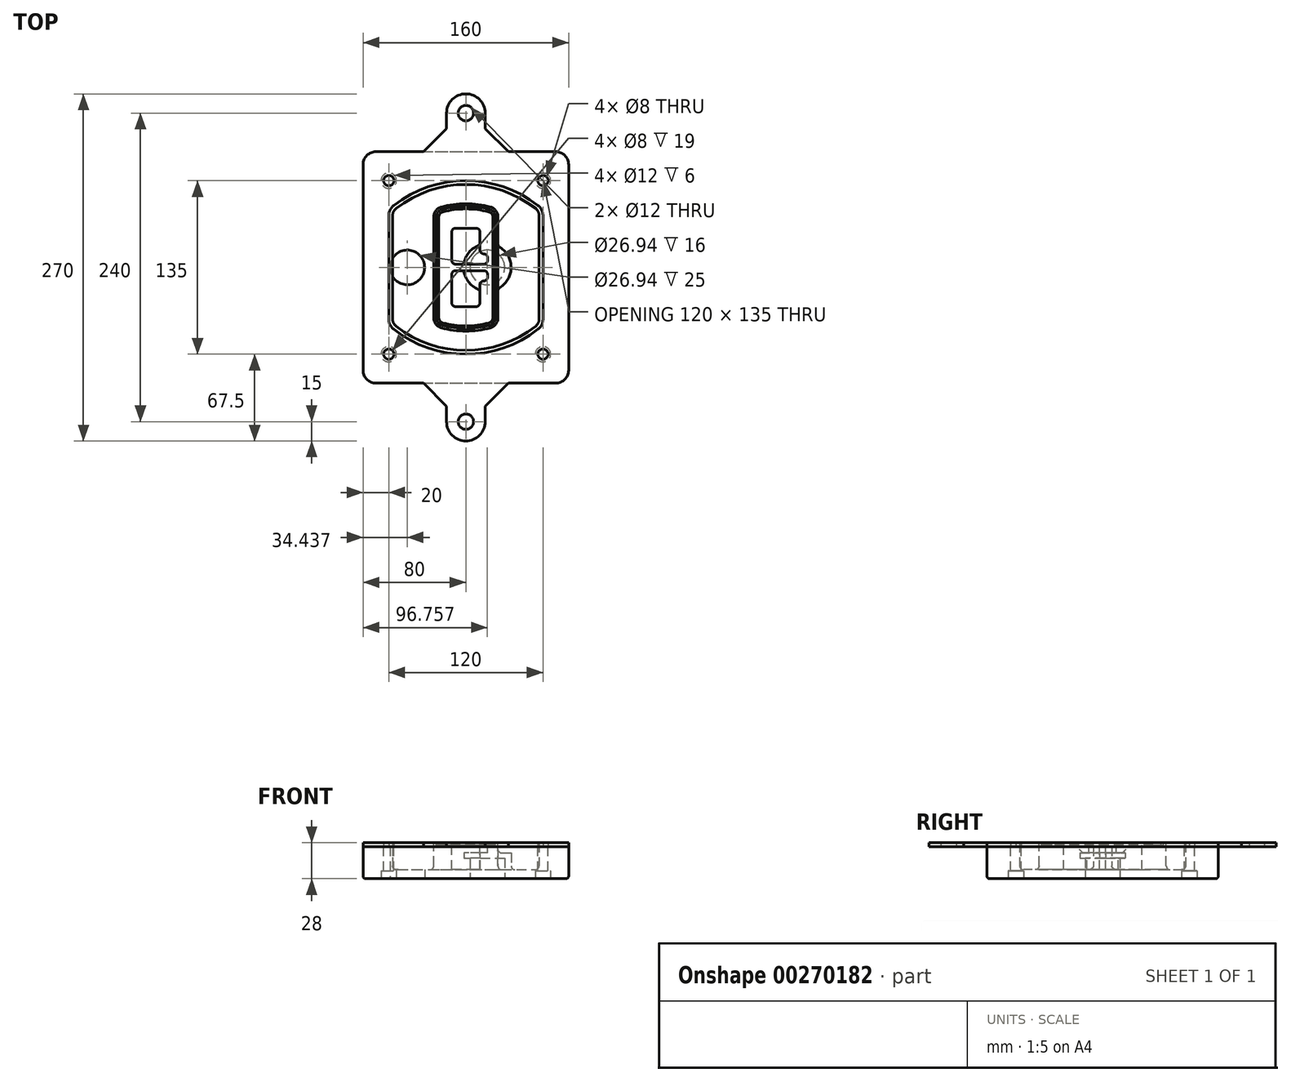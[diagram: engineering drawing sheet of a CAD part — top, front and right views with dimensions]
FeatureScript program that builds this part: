
annotation { "Feature Type Name" : "Feature", "Feature Type Description" : "" }
export const myFeature = defineFeature(function(context is Context, id is Id, definition is map)
    precondition{}
    {
        {
            var Q0;
            Q0=qCreatedBy(makeId("Top.planeOp"),FACE);
            var sketch = newSketch(context, id + "F0", { "sketchPlane" : qUnion([Q0])});
            skPoint(sketch, "E0.rect.middle", {"position": v(0, 0) * mm});
            skLineSegment(sketch, "E1.bottom", {"start": v(-70, -90) * mm, "end": v(70, -90) * mm});
            skLineSegment(sketch, "E1.top", {"start": v(-70, 90) * mm, "end": v(70, 90) * mm});
            skLineSegment(sketch, "E1.left", {"start": v(-80, -80) * mm, "end": v(-80, 80) * mm});
            skLineSegment(sketch, "E1.right", {"start": v(80, -80) * mm, "end": v(80, 80) * mm});
            skLineSegment(sketch, "E2", {"start": v(-80, 90) * mm, "end": v(80, -90) * mm, "construction": true});
            skLineSegment(sketch, "E3", {"start": v(80, 90) * mm, "end": v(-80, -90) * mm, "construction": true});
            skCircle(sketch, "E4", {"center": v(-60, 67.5) * mm, "radius": 4 * mm});
            skCircle(sketch, "E5", {"center": v(60, 67.5) * mm, "radius": 4 * mm});
            skCircle(sketch, "E6", {"center": v(60, -67.5) * mm, "radius": 4 * mm});
            skCircle(sketch, "E7", {"center": v(-60, -67.5) * mm, "radius": 4 * mm});
            skLineSegment(sketch, "E8", {"start": v(-60, 67.5) * mm, "end": v(60, 67.5) * mm, "construction": true});
            skLineSegment(sketch, "E9", {"start": v(60, 67.5) * mm, "end": v(60, -67.5) * mm, "construction": true});
            skLineSegment(sketch, "E10", {"start": v(60, -67.5) * mm, "end": v(-60, -67.5) * mm, "construction": true});
            skLineSegment(sketch, "E11", {"start": v(-60, -67.5) * mm, "end": v(-60, 67.5) * mm, "construction": true});
            skLineSegment(sketch, "E12", {"start": v(-60, 40.3) * mm, "end": v(-60, -40.3) * mm});
            skLineSegment(sketch, "E13", {"start": v(60, 40.3) * mm, "end": v(60, -40.3) * mm});
            skArc(sketch, "E14", {"start": v(56.15, 48.18) * mm, "mid": v(0, 67.5) * mm, "end": v(-56.15, 48.18) * mm});
            skArc(sketch, "E15", {"start": v(-56.15, -48.18) * mm, "mid": v(0, -67.5) * mm, "end": v(56.15, -48.18) * mm});
            skLineSegment(sketch, "E16", {"start": v(-60, 0) * mm, "end": v(60, 0) * mm, "construction": true});
            skPoint(sketch, "E17.visualSharp", {"position": v(-60, -45) * mm});
            skArc(sketch, "E17.filletArc", {"start": v(-60, -40.3) * mm, "mid": v(-58.99, -44.68) * mm, "end": v(-56.15, -48.18) * mm});
            skPoint(sketch, "E18.visualSharp", {"position": v(-60, 45) * mm});
            skArc(sketch, "E18.filletArc", {"start": v(-56.15, 48.18) * mm, "mid": v(-58.99, 44.68) * mm, "end": v(-60, 40.3) * mm});
            skPoint(sketch, "E19.visualSharp", {"position": v(60, 45) * mm});
            skArc(sketch, "E19.filletArc", {"start": v(60, 40.3) * mm, "mid": v(58.99, 44.68) * mm, "end": v(56.15, 48.18) * mm});
            skPoint(sketch, "E20.visualSharp", {"position": v(60, -45) * mm});
            skArc(sketch, "E20.filletArc", {"start": v(56.15, -48.18) * mm, "mid": v(58.99, -44.68) * mm, "end": v(60, -40.3) * mm});
            skPoint(sketch, "E21.visualSharp", {"position": v(-80, 90) * mm});
            skArc(sketch, "E21.filletArc", {"start": v(-70, 90) * mm, "mid": v(-77.07, 87.07) * mm, "end": v(-80, 80) * mm});
            skPoint(sketch, "E22.visualSharp", {"position": v(80, 90) * mm});
            skArc(sketch, "E22.filletArc", {"start": v(80, 80) * mm, "mid": v(77.07, 87.07) * mm, "end": v(70, 90) * mm});
            skPoint(sketch, "E23.visualSharp", {"position": v(80, -90) * mm});
            skArc(sketch, "E23.filletArc", {"start": v(70, -90) * mm, "mid": v(77.07, -87.07) * mm, "end": v(80, -80) * mm});
            skPoint(sketch, "E24.visualSharp", {"position": v(-80, -90) * mm});
            skArc(sketch, "E24.filletArc", {"start": v(-80, -80) * mm, "mid": v(-77.07, -87.07) * mm, "end": v(-70, -90) * mm});
            skArc(sketch, "E25.0", {"start": v(57, 40.3) * mm, "mid": v(56.3, 43.36) * mm, "end": v(54.3, 45.81) * mm});
            skLineSegment(sketch, "E25.1", {"start": v(57, 40.3) * mm, "end": v(57, -40.3) * mm});
            skArc(sketch, "E25.2", {"start": v(54.3, -45.81) * mm, "mid": v(56.3, -43.36) * mm, "end": v(57, -40.3) * mm});
            skArc(sketch, "E25.3", {"start": v(-54.3, -45.81) * mm, "mid": v(0, -64.5) * mm, "end": v(54.3, -45.81) * mm});
            skArc(sketch, "E25.4", {"start": v(-57, -40.3) * mm, "mid": v(-56.3, -43.36) * mm, "end": v(-54.3, -45.81) * mm});
            skArc(sketch, "E25.5", {"start": v(54.3, 45.81) * mm, "mid": v(0, 64.5) * mm, "end": v(-54.3, 45.81) * mm});
            skLineSegment(sketch, "E25.6", {"start": v(-57, 40.3) * mm, "end": v(-57, -40.3) * mm});
            skArc(sketch, "E25.7", {"start": v(-54.3, 45.81) * mm, "mid": v(-56.3, 43.36) * mm, "end": v(-57, 40.3) * mm});
            skArc(sketch, "E26.0", {"start": v(-58.62, 51.33) * mm, "mid": v(-62.58, 46.43) * mm, "end": v(-64, 40.3) * mm});
            skArc(sketch, "E26.1", {"start": v(58.62, 51.33) * mm, "mid": v(0, 71.5) * mm, "end": v(-58.62, 51.33) * mm});
            skArc(sketch, "E26.2", {"start": v(64, 40.3) * mm, "mid": v(62.58, 46.43) * mm, "end": v(58.62, 51.33) * mm});
            skLineSegment(sketch, "E26.3", {"start": v(64, 40.3) * mm, "end": v(64, -40.3) * mm});
            skArc(sketch, "E26.4", {"start": v(58.62, -51.33) * mm, "mid": v(62.58, -46.43) * mm, "end": v(64, -40.3) * mm});
            skLineSegment(sketch, "E26.5", {"start": v(-64, 40.3) * mm, "end": v(-64, -40.3) * mm});
            skArc(sketch, "E26.6", {"start": v(-58.62, -51.33) * mm, "mid": v(0, -71.5) * mm, "end": v(58.62, -51.33) * mm});
            skArc(sketch, "E26.7", {"start": v(-64, -40.3) * mm, "mid": v(-62.58, -46.43) * mm, "end": v(-58.62, -51.33) * mm});
            skSolve(sketch);
        }
        {
            var Q0;
            Q0=makeQuery(id+"F0.imprint","IMPRINT",FACE,{"disambiguationData":[TD([[makeQuery(id+"F0.imprint","IMPRINT",EDGE,{"derivedFrom":sQuery(id+"F0.wireOp",EDGE,"E1.bottom")}),1.0]])]});
            var Q1;
            Q1=makeQuery(id+"F0.imprint","IMPRINT",FACE,{"disambiguationData":[TD([[makeQuery(id+"F0.imprint","IMPRINT",EDGE,{"derivedFrom":sQuery(id+"F0.wireOp",EDGE,"E12")}),1.0]])]});
            var Q2;
            Q2=makeQuery(id+"F0.imprint","IMPRINT",FACE,{"disambiguationData":[TD([[makeQuery(id+"F0.imprint","IMPRINT",EDGE,{"derivedFrom":sQuery(id+"F0.wireOp",EDGE,"E25.0")}),1.0]])]});
            var Q3;
            Q3=makeQuery(id+"F0.imprint","IMPRINT",FACE,{"disambiguationData":[TD([[makeQuery(id+"F0.imprint","IMPRINT",EDGE,{"derivedFrom":sQuery(id+"F0.wireOp",EDGE,"E12")}),-1.0]])]});
            extrude(context, id + "F1", {"entities" : qUnion([Q0, Q1, Q2, Q3]), "oppositeDirection" : true, "depth" : 25 * mm});
        }
        {
            var Q0;
            Q0=makeQuery(id+"F0.imprint","IMPRINT",FACE,{"disambiguationData":[TD([[makeQuery(id+"F0.imprint","IMPRINT",EDGE,{"derivedFrom":sQuery(id+"F0.wireOp",EDGE,"E12")}),1.0]])]});
            extrude(context, id + "F2", {"entities" : qUnion([Q0]), "operationType" : NewBodyOperationType.ADD, "depth" : 3 * mm});
        }
        {
            var Q0;
            Q0=makeQuery(id+"F0.imprint","IMPRINT",FACE,{"disambiguationData":[TD([[makeQuery(id+"F0.imprint","IMPRINT",EDGE,{"derivedFrom":sQuery(id+"F0.wireOp",EDGE,"E25.0")}),1.0]])]});
            extrude(context, id + "F3", {"entities" : qUnion([Q0]), "operationType" : NewBodyOperationType.REMOVE, "oppositeDirection" : true, "depth" : 18 * mm});
        }
        {
            var Q0;
            Q0=makeQuery(id+"F2.opExtrude","CAP_FACE",FACE,{"disambiguationData":[OSD([sQuery(id+"F0.wireOp",EDGE,"E12"),sQuery(id+"F0.wireOp",EDGE,"E13"),sQuery(id+"F0.wireOp",EDGE,"E14"),sQuery(id+"F0.wireOp",EDGE,"E15"),sQuery(id+"F0.wireOp",EDGE,"E17.filletArc"),sQuery(id+"F0.wireOp",EDGE,"E18.filletArc"),sQuery(id+"F0.wireOp",EDGE,"E19.filletArc"),sQuery(id+"F0.wireOp",EDGE,"E20.filletArc"),sQuery(id+"F0.wireOp",EDGE,"E25.0"),sQuery(id+"F0.wireOp",EDGE,"E25.1"),sQuery(id+"F0.wireOp",EDGE,"E25.2"),sQuery(id+"F0.wireOp",EDGE,"E25.3"),sQuery(id+"F0.wireOp",EDGE,"E25.4"),sQuery(id+"F0.wireOp",EDGE,"E25.5"),sQuery(id+"F0.wireOp",EDGE,"E25.6"),sQuery(id+"F0.wireOp",EDGE,"E25.7")])],"isStart":false});
            var sketch = newSketch(context, id + "F4", { "sketchPlane" : qUnion([Q0])});
            skArc(sketch, "E27.0", {"start": v(-19.08, -46.97) * mm, "mid": v(0, -49.5) * mm, "end": v(19.08, -46.97) * mm});
            skArc(sketch, "E28.0", {"start": v(19.08, 46.97) * mm, "mid": v(0, 49.5) * mm, "end": v(-19.08, 46.97) * mm});
            skLineSegment(sketch, "E29", {"start": v(-25, 39.25) * mm, "end": v(-25, -39.25) * mm});
            skLineSegment(sketch, "E30", {"start": v(25, 39.25) * mm, "end": v(25, -39.25) * mm});
            skLineSegment(sketch, "E31", {"start": v(-25, 45.1) * mm, "end": v(25, 45.1) * mm, "construction": true});
            skLineSegment(sketch, "E32", {"start": v(-25, -45.1) * mm, "end": v(25, -45.1) * mm, "construction": true});
            skPoint(sketch, "E33.visualSharp", {"position": v(-25, 45.1) * mm});
            skArc(sketch, "E33.filletArc", {"start": v(-19.08, 46.97) * mm, "mid": v(-23.35, 44.11) * mm, "end": v(-25, 39.25) * mm});
            skPoint(sketch, "E34.visualSharp", {"position": v(25, 45.1) * mm});
            skArc(sketch, "E34.filletArc", {"start": v(25, 39.25) * mm, "mid": v(23.35, 44.11) * mm, "end": v(19.08, 46.97) * mm});
            skPoint(sketch, "E35.visualSharp", {"position": v(25, -45.1) * mm});
            skArc(sketch, "E35.filletArc", {"start": v(19.08, -46.97) * mm, "mid": v(23.35, -44.11) * mm, "end": v(25, -39.25) * mm});
            skPoint(sketch, "E36.visualSharp", {"position": v(-25, -45.1) * mm});
            skArc(sketch, "E36.filletArc", {"start": v(-25, -39.25) * mm, "mid": v(-23.35, -44.11) * mm, "end": v(-19.08, -46.97) * mm});
            skArc(sketch, "E37.0", {"start": v(54.3, 45.81) * mm, "mid": v(0, 64.5) * mm, "end": v(-54.3, 45.81) * mm});
            skArc(sketch, "E37.1", {"start": v(-54.3, 45.81) * mm, "mid": v(-56.3, 43.36) * mm, "end": v(-57, 40.3) * mm});
            skLineSegment(sketch, "E37.2", {"start": v(-57, 40.3) * mm, "end": v(-57, -40.3) * mm});
            skArc(sketch, "E37.3", {"start": v(-57, -40.3) * mm, "mid": v(-56.3, -43.36) * mm, "end": v(-54.3, -45.81) * mm});
            skArc(sketch, "E37.4", {"start": v(-54.3, -45.81) * mm, "mid": v(0, -64.5) * mm, "end": v(54.3, -45.81) * mm});
            skArc(sketch, "E37.5", {"start": v(54.3, -45.81) * mm, "mid": v(56.3, -43.36) * mm, "end": v(57, -40.3) * mm});
            skLineSegment(sketch, "E37.6", {"start": v(57, 40.3) * mm, "end": v(57, -40.3) * mm});
            skArc(sketch, "E37.7", {"start": v(57, 40.3) * mm, "mid": v(56.3, 43.36) * mm, "end": v(54.3, 45.81) * mm});
            skLineSegment(sketch, "E38.0", {"start": v(23, 39.25) * mm, "end": v(23, -39.25) * mm});
            skArc(sketch, "E38.1", {"start": v(18.56, -45.04) * mm, "mid": v(21.76, -42.9) * mm, "end": v(23, -39.25) * mm});
            skArc(sketch, "E38.2", {"start": v(-18.56, -45.04) * mm, "mid": v(0, -47.5) * mm, "end": v(18.56, -45.04) * mm});
            skArc(sketch, "E38.3", {"start": v(-23, -39.25) * mm, "mid": v(-21.76, -42.9) * mm, "end": v(-18.56, -45.04) * mm});
            skLineSegment(sketch, "E38.4", {"start": v(-23, 39.25) * mm, "end": v(-23, -39.25) * mm});
            skArc(sketch, "E38.5", {"start": v(23, 39.25) * mm, "mid": v(21.76, 42.9) * mm, "end": v(18.56, 45.04) * mm});
            skArc(sketch, "E38.6", {"start": v(-18.56, 45.04) * mm, "mid": v(-21.76, 42.9) * mm, "end": v(-23, 39.25) * mm});
            skArc(sketch, "E38.7", {"start": v(18.56, 45.04) * mm, "mid": v(0, 47.5) * mm, "end": v(-18.56, 45.04) * mm});
            skArc(sketch, "E39.0", {"start": v(21, 39.25) * mm, "mid": v(20.18, 41.68) * mm, "end": v(18.04, 43.1) * mm});
            skLineSegment(sketch, "E39.1", {"start": v(21, 39.25) * mm, "end": v(21, -39.25) * mm});
            skArc(sketch, "E39.2", {"start": v(18.04, -43.1) * mm, "mid": v(20.18, -41.68) * mm, "end": v(21, -39.25) * mm});
            skArc(sketch, "E39.3", {"start": v(-18.04, -43.1) * mm, "mid": v(0, -45.5) * mm, "end": v(18.04, -43.1) * mm});
            skArc(sketch, "E39.4", {"start": v(-21, -39.25) * mm, "mid": v(-20.18, -41.68) * mm, "end": v(-18.04, -43.1) * mm});
            skArc(sketch, "E39.5", {"start": v(18.04, 43.1) * mm, "mid": v(0, 45.5) * mm, "end": v(-18.04, 43.1) * mm});
            skLineSegment(sketch, "E39.6", {"start": v(-21, 39.25) * mm, "end": v(-21, -39.25) * mm});
            skArc(sketch, "E39.7", {"start": v(-18.04, 43.1) * mm, "mid": v(-20.18, 41.68) * mm, "end": v(-21, 39.25) * mm});
            skLineSegment(sketch, "E40", {"start": v(-25, 0) * mm, "end": v(25, 0) * mm, "construction": true});
            skLineSegment(sketch, "E41", {"start": v(-11, 5.5) * mm, "end": v(-11, 27.5) * mm});
            skLineSegment(sketch, "E42", {"start": v(-8, 30.5) * mm, "end": v(8, 30.5) * mm});
            skLineSegment(sketch, "E43", {"start": v(11, 27.5) * mm, "end": v(11, 13.5) * mm});
            skLineSegment(sketch, "E44", {"start": v(14, 10.5) * mm, "end": v(14, 10.5) * mm});
            skLineSegment(sketch, "E45", {"start": v(17, 7.5) * mm, "end": v(17, 5.5) * mm});
            skLineSegment(sketch, "E46", {"start": v(14, 2.5) * mm, "end": v(-8, 2.5) * mm});
            skPoint(sketch, "E47.visualSharp", {"position": v(-11, 30.5) * mm});
            skArc(sketch, "E47.filletArc", {"start": v(-8, 30.5) * mm, "mid": v(-10.12, 29.62) * mm, "end": v(-11, 27.5) * mm});
            skPoint(sketch, "E48.visualSharp", {"position": v(11, 30.5) * mm});
            skArc(sketch, "E48.filletArc", {"start": v(11, 27.5) * mm, "mid": v(10.12, 29.62) * mm, "end": v(8, 30.5) * mm});
            skPoint(sketch, "E49.visualSharp", {"position": v(11, 10.5) * mm});
            skArc(sketch, "E49.filletArc", {"start": v(11, 13.5) * mm, "mid": v(11.88, 11.38) * mm, "end": v(14, 10.5) * mm});
            skPoint(sketch, "E50.visualSharp", {"position": v(17, 10.5) * mm});
            skArc(sketch, "E50.filletArc", {"start": v(17, 7.5) * mm, "mid": v(16.12, 9.62) * mm, "end": v(14, 10.5) * mm});
            skPoint(sketch, "E51.visualSharp", {"position": v(17, 2.5) * mm});
            skArc(sketch, "E51.filletArc", {"start": v(14, 2.5) * mm, "mid": v(16.12, 3.38) * mm, "end": v(17, 5.5) * mm});
            skPoint(sketch, "E52.visualSharp", {"position": v(-11, 2.5) * mm});
            skArc(sketch, "E52.filletArc", {"start": v(-11, 5.5) * mm, "mid": v(-10.12, 3.38) * mm, "end": v(-8, 2.5) * mm});
            skLineSegment(sketch, "E53.0.MirrorCS", {"start": v(14, -2.5) * mm, "end": v(-8, -2.5) * mm});
            skArc(sketch, "E54.0.MirrorCS", {"start": v(-11, -5.5) * mm, "mid": v(-10.12, -3.38) * mm, "end": v(-8, -2.5) * mm});
            skLineSegment(sketch, "E55.0.MirrorCS", {"start": v(-11, -5.5) * mm, "end": v(-11, -27.5) * mm});
            skArc(sketch, "E56.0.MirrorCS", {"start": v(-8, -30.5) * mm, "mid": v(-10.12, -29.62) * mm, "end": v(-11, -27.5) * mm});
            skLineSegment(sketch, "E57.0.MirrorCS", {"start": v(-8, -30.5) * mm, "end": v(8, -30.5) * mm});
            skArc(sketch, "E58.0.MirrorCS", {"start": v(11, -27.5) * mm, "mid": v(10.12, -29.62) * mm, "end": v(8, -30.5) * mm});
            skLineSegment(sketch, "E59.0.MirrorCS", {"start": v(11, -27.5) * mm, "end": v(11, -13.5) * mm});
            skArc(sketch, "E60.0.MirrorCS", {"start": v(11, -13.5) * mm, "mid": v(11.88, -11.38) * mm, "end": v(14, -10.5) * mm});
            skArc(sketch, "E61.0.MirrorCS", {"start": v(17, -7.5) * mm, "mid": v(16.12, -9.62) * mm, "end": v(14, -10.5) * mm});
            skLineSegment(sketch, "E62.0.MirrorCS", {"start": v(17, -7.5) * mm, "end": v(17, -5.5) * mm});
            skArc(sketch, "E63.0.MirrorCS", {"start": v(14, -2.5) * mm, "mid": v(16.12, -3.38) * mm, "end": v(17, -5.5) * mm});
            skSolve(sketch);
        }
        {
            var Q0;
            Q0=makeQuery(id+"F4.imprint","IMPRINT",FACE,{"disambiguationData":[TD([[makeQuery(id+"F4.imprint","IMPRINT",EDGE,{"derivedFrom":sQuery(id+"F4.wireOp",EDGE,"E27.0")}),1.0]])]});
            var Q1;
            Q1=makeQuery(id+"F4.imprint","IMPRINT",FACE,{"disambiguationData":[TD([[makeQuery(id+"F4.imprint","IMPRINT",EDGE,{"derivedFrom":sQuery(id+"F4.wireOp",EDGE,"E38.0")}),-1.0]])]});
            var Q2;
            Q2=makeQuery(id+"F4.imprint","IMPRINT",FACE,{"disambiguationData":[TD([[makeQuery(id+"F4.imprint","IMPRINT",EDGE,{"derivedFrom":sQuery(id+"F4.wireOp",EDGE,"E39.0")}),1.0]])]});
            extrude(context, id + "F5", {"entities" : qUnion([Q0, Q1, Q2]), "operationType" : NewBodyOperationType.ADD, "endBound" : BoundingType.UP_TO_NEXT, "oppositeDirection" : true, "depth" : 25 * mm});
        }
        {
            var Q0;
            Q0=makeQuery(id+"F4.imprint","IMPRINT",FACE,{"disambiguationData":[TD([[makeQuery(id+"F4.imprint","IMPRINT",EDGE,{"derivedFrom":sQuery(id+"F4.wireOp",EDGE,"E38.0")}),-1.0]])]});
            extrude(context, id + "F6", {"entities" : qUnion([Q0]), "operationType" : NewBodyOperationType.REMOVE, "oppositeDirection" : true, "depth" : 2 * mm});
        }
        {
            var Q0;
            Q0=makeQuery(id+"F1.opExtrude","CAP_FACE",FACE,{"disambiguationData":[OSD([sQuery(id+"F0.wireOp",EDGE,"E1.bottom"),sQuery(id+"F0.wireOp",EDGE,"E1.top"),sQuery(id+"F0.wireOp",EDGE,"E1.left"),sQuery(id+"F0.wireOp",EDGE,"E1.right"),sQuery(id+"F0.wireOp",EDGE,"E4"),sQuery(id+"F0.wireOp",EDGE,"E5"),sQuery(id+"F0.wireOp",EDGE,"E6"),sQuery(id+"F0.wireOp",EDGE,"E7"),sQuery(id+"F0.wireOp",EDGE,"E21.filletArc"),sQuery(id+"F0.wireOp",EDGE,"E22.filletArc"),sQuery(id+"F0.wireOp",EDGE,"E23.filletArc"),sQuery(id+"F0.wireOp",EDGE,"E24.filletArc")])],"isStart":false});
            var sketch = newSketch(context, id + "F7", { "sketchPlane" : qUnion([Q0])});
            skCircle(sketch, "E64", {"center": v(16.76, 0) * mm, "radius": 13.47 * mm});
            skCircle(sketch, "E65", {"center": v(-45.56, 0) * mm, "radius": 13.47 * mm});
            skLineSegment(sketch, "E66", {"start": v(80, 0) * mm, "end": v(-80, 0) * mm});
            skCircle(sketch, "E67", {"center": v(16.76, 0) * mm, "radius": 18.47 * mm});
            skCircle(sketch, "E68", {"center": v(60, -67.5) * mm, "radius": 6 * mm});
            skCircle(sketch, "E69", {"center": v(-60, -67.5) * mm, "radius": 6 * mm});
            skCircle(sketch, "E70", {"center": v(-60, 67.5) * mm, "radius": 6 * mm});
            skCircle(sketch, "E71", {"center": v(60, 67.5) * mm, "radius": 6 * mm});
            skSolve(sketch);
        }
        {
            var Q0;
            {var subQ1=sQuery(id+"F7.wireOp",EDGE,"E66");var subQ4=sQuery(id+"F7.wireOp",EDGE,"E64");var subQ6=makeQuery(id+"F7.imprint","INTERSECT",VERTEX,{"disambiguationData":[OD(0.0)],"derivedFrom":[subQ4,subQ1]});Q0=makeQuery(id+"F7.imprint","IMPRINT",FACE,{"disambiguationData":[TD([[makeQuery(id+"F7.imprint","IMPRINT",EDGE,{"disambiguationData":[TD([[subQ6,-1.0]])],"derivedFrom":subQ4}),-1.0]])]});}
            var Q1;
            {var subQ0=sQuery(id+"F7.wireOp",EDGE,"E66");var subQ1=sQuery(id+"F7.wireOp",EDGE,"E64");var subQ3=makeQuery(id+"F7.imprint","INTERSECT",VERTEX,{"disambiguationData":[OD(0.0)],"derivedFrom":[subQ1,subQ0]});Q1=makeQuery(id+"F7.imprint","IMPRINT",FACE,{"disambiguationData":[TD([[makeQuery(id+"F7.imprint","IMPRINT",EDGE,{"disambiguationData":[TD([[subQ3,-1.0]])],"derivedFrom":subQ1}),1.0]])]});}
            var Q2;
            {var subQ0=sQuery(id+"F7.wireOp",EDGE,"E66");var subQ1=sQuery(id+"F7.wireOp",EDGE,"E64");var subQ3=makeQuery(id+"F7.imprint","INTERSECT",VERTEX,{"disambiguationData":[OD(0.0)],"derivedFrom":[subQ1,subQ0]});Q2=makeQuery(id+"F7.imprint","IMPRINT",FACE,{"disambiguationData":[TD([[makeQuery(id+"F7.imprint","IMPRINT",EDGE,{"disambiguationData":[TD([[subQ3,1.0]])],"derivedFrom":subQ1}),1.0]])]});}
            var Q3;
            {var subQ1=sQuery(id+"F7.wireOp",EDGE,"E66");var subQ4=sQuery(id+"F7.wireOp",EDGE,"E64");var subQ6=makeQuery(id+"F7.imprint","INTERSECT",VERTEX,{"disambiguationData":[OD(0.0)],"derivedFrom":[subQ4,subQ1]});Q3=makeQuery(id+"F7.imprint","IMPRINT",FACE,{"disambiguationData":[TD([[makeQuery(id+"F7.imprint","IMPRINT",EDGE,{"disambiguationData":[TD([[subQ6,1.0]])],"derivedFrom":subQ4}),-1.0]])]});}
            extrude(context, id + "F8", {"entities" : qUnion([Q0, Q1, Q2, Q3]), "operationType" : NewBodyOperationType.ADD, "oppositeDirection" : true, "depth" : 20 * mm});
        }
        {
            var Q0;
            {var subQ0=sQuery(id+"F7.wireOp",EDGE,"E66");var subQ1=sQuery(id+"F7.wireOp",EDGE,"E64");var subQ3=makeQuery(id+"F7.imprint","INTERSECT",VERTEX,{"disambiguationData":[OD(0.0)],"derivedFrom":[subQ1,subQ0]});Q0=makeQuery(id+"F7.imprint","IMPRINT",FACE,{"disambiguationData":[TD([[makeQuery(id+"F7.imprint","IMPRINT",EDGE,{"disambiguationData":[TD([[subQ3,-1.0]])],"derivedFrom":subQ1}),1.0]])]});}
            var Q1;
            {var subQ0=sQuery(id+"F7.wireOp",EDGE,"E66");var subQ1=sQuery(id+"F7.wireOp",EDGE,"E64");var subQ3=makeQuery(id+"F7.imprint","INTERSECT",VERTEX,{"disambiguationData":[OD(0.0)],"derivedFrom":[subQ1,subQ0]});Q1=makeQuery(id+"F7.imprint","IMPRINT",FACE,{"disambiguationData":[TD([[makeQuery(id+"F7.imprint","IMPRINT",EDGE,{"disambiguationData":[TD([[subQ3,1.0]])],"derivedFrom":subQ1}),1.0]])]});}
            extrude(context, id + "F9", {"entities" : qUnion([Q0, Q1]), "operationType" : NewBodyOperationType.REMOVE, "oppositeDirection" : true, "depth" : 16 * mm});
        }
        {
            var Q0;
            {var subQ0=sQuery(id+"F7.wireOp",EDGE,"E66");var subQ1=sQuery(id+"F7.wireOp",EDGE,"E65");var subQ3=makeQuery(id+"F7.imprint","INTERSECT",VERTEX,{"disambiguationData":[OD(0.0)],"derivedFrom":[subQ1,subQ0]});Q0=makeQuery(id+"F7.imprint","IMPRINT",FACE,{"disambiguationData":[TD([[makeQuery(id+"F7.imprint","IMPRINT",EDGE,{"disambiguationData":[TD([[subQ3,-1.0]])],"derivedFrom":subQ1}),1.0]])]});}
            var Q1;
            {var subQ0=sQuery(id+"F7.wireOp",EDGE,"E66");var subQ1=sQuery(id+"F7.wireOp",EDGE,"E65");var subQ3=makeQuery(id+"F7.imprint","INTERSECT",VERTEX,{"disambiguationData":[OD(0.0)],"derivedFrom":[subQ1,subQ0]});Q1=makeQuery(id+"F7.imprint","IMPRINT",FACE,{"disambiguationData":[TD([[makeQuery(id+"F7.imprint","IMPRINT",EDGE,{"disambiguationData":[TD([[subQ3,1.0]])],"derivedFrom":subQ1}),1.0]])]});}
            extrude(context, id + "F10", {"entities" : qUnion([Q0, Q1]), "operationType" : NewBodyOperationType.REMOVE, "oppositeDirection" : true, "depth" : 25 * mm});
        }
        {
            var Q0;
            Q0=makeQuery(id+"F7.imprint","IMPRINT",FACE,{"disambiguationData":[TD([[makeQuery(id+"F7.imprint","IMPRINT",EDGE,{"derivedFrom":sQuery(id+"F7.wireOp",EDGE,"E68")}),1.0]])]});
            var Q1;
            Q1=makeQuery(id+"F7.imprint","IMPRINT",FACE,{"disambiguationData":[TD([[makeQuery(id+"F7.imprint","IMPRINT",EDGE,{"derivedFrom":makeQuery(id+"F1.opExtrude","CAP_EDGE",EDGE,{"disambiguationData":[OSD([sQuery(id+"F0.wireOp",EDGE,"E5")])],"isStart":false})}),-1.0]])]});
            var Q2;
            Q2=makeQuery(id+"F7.imprint","IMPRINT",FACE,{"disambiguationData":[TD([[makeQuery(id+"F7.imprint","IMPRINT",EDGE,{"derivedFrom":sQuery(id+"F7.wireOp",EDGE,"E69")}),1.0]])]});
            var Q3;
            Q3=makeQuery(id+"F7.imprint","IMPRINT",FACE,{"disambiguationData":[TD([[makeQuery(id+"F7.imprint","IMPRINT",EDGE,{"derivedFrom":makeQuery(id+"F1.opExtrude","CAP_EDGE",EDGE,{"disambiguationData":[OSD([sQuery(id+"F0.wireOp",EDGE,"E4")])],"isStart":false})}),-1.0]])]});
            var Q4;
            Q4=makeQuery(id+"F7.imprint","IMPRINT",FACE,{"disambiguationData":[TD([[makeQuery(id+"F7.imprint","IMPRINT",EDGE,{"derivedFrom":sQuery(id+"F7.wireOp",EDGE,"E70")}),1.0]])]});
            var Q5;
            Q5=makeQuery(id+"F7.imprint","IMPRINT",FACE,{"disambiguationData":[TD([[makeQuery(id+"F7.imprint","IMPRINT",EDGE,{"derivedFrom":makeQuery(id+"F1.opExtrude","CAP_EDGE",EDGE,{"disambiguationData":[OSD([sQuery(id+"F0.wireOp",EDGE,"E7")])],"isStart":false})}),-1.0]])]});
            var Q6;
            Q6=makeQuery(id+"F7.imprint","IMPRINT",FACE,{"disambiguationData":[TD([[makeQuery(id+"F7.imprint","IMPRINT",EDGE,{"derivedFrom":sQuery(id+"F7.wireOp",EDGE,"E71")}),1.0]])]});
            var Q7;
            Q7=makeQuery(id+"F7.imprint","IMPRINT",FACE,{"disambiguationData":[TD([[makeQuery(id+"F7.imprint","IMPRINT",EDGE,{"derivedFrom":makeQuery(id+"F1.opExtrude","CAP_EDGE",EDGE,{"disambiguationData":[OSD([sQuery(id+"F0.wireOp",EDGE,"E6")])],"isStart":false})}),-1.0]])]});
            extrude(context, id + "F11", {"entities" : qUnion([Q0, Q1, Q2, Q3, Q4, Q5, Q6, Q7]), "operationType" : NewBodyOperationType.REMOVE, "oppositeDirection" : true, "depth" : 6 * mm});
        }
        {
            var Q0;
            Q0=makeQuery(id+"F9.boolean.opBoolean","COPY",FACE,{"derivedFrom":makeQuery(id+"F9.opExtrude","CAP_FACE",FACE,{"disambiguationData":[OSD([sQuery(id+"F7.wireOp",EDGE,"E64")])],"isStart":false})});
            var sketch = newSketch(context, id + "F12", { "sketchPlane" : qUnion([Q0])});
            skArc(sketch, "E72.0", {"start": v(11, 17.55) * mm, "mid": v(2.57, 11.82) * mm, "end": v(-1.54, 2.5) * mm});
            skArc(sketch, "E72.1", {"start": v(-1.54, -2.5) * mm, "mid": v(2.57, -11.82) * mm, "end": v(11, -17.55) * mm});
            skLineSegment(sketch, "E73", {"start": v(-1.54, -2.5) * mm, "end": v(14, -2.5) * mm});
            skLineSegment(sketch, "E74.0", {"start": v(14, 2.5) * mm, "end": v(-1.54, 2.5) * mm});
            skArc(sketch, "E74.1", {"start": v(14, 2.5) * mm, "mid": v(16.12, 3.38) * mm, "end": v(17, 5.5) * mm});
            skLineSegment(sketch, "E74.2", {"start": v(17, 7.5) * mm, "end": v(17, 5.5) * mm});
            skArc(sketch, "E74.3", {"start": v(17, 7.5) * mm, "mid": v(16.12, 9.62) * mm, "end": v(14, 10.5) * mm});
            skArc(sketch, "E74.4", {"start": v(11, 13.5) * mm, "mid": v(11.88, 11.38) * mm, "end": v(14, 10.5) * mm});
            skLineSegment(sketch, "E74.5", {"start": v(11, 17.55) * mm, "end": v(11, 13.5) * mm});
            skLineSegment(sketch, "E74.7", {"start": v(14, -2.5) * mm, "end": v(-1.54, -2.5) * mm});
            skArc(sketch, "E74.8", {"start": v(14, -2.5) * mm, "mid": v(16.12, -3.38) * mm, "end": v(17, -5.5) * mm});
            skLineSegment(sketch, "E74.9", {"start": v(17, -7.5) * mm, "end": v(17, -5.5) * mm});
            skArc(sketch, "E74.10", {"start": v(17, -7.5) * mm, "mid": v(16.12, -9.62) * mm, "end": v(14, -10.5) * mm});
            skArc(sketch, "E74.11", {"start": v(11, -13.5) * mm, "mid": v(11.88, -11.38) * mm, "end": v(14, -10.5) * mm});
            skLineSegment(sketch, "E74.12", {"start": v(11, -17.55) * mm, "end": v(11, -13.5) * mm});
            skPoint(sketch, "E75.orphan", {"position": v(11, -27.5) * mm});
            skPoint(sketch, "E76.orphan", {"position": v(-8, -2.5) * mm});
            skPoint(sketch, "E77.orphan", {"position": v(-8, 2.5) * mm});
            skPoint(sketch, "E78.orphan", {"position": v(11, 27.5) * mm});
            skSolve(sketch);
        }
        {
            var Q0;
            {var subQ7=sQuery(id+"F12.wireOp",EDGE,"E72.0");var subQ14=sQuery(id+"F12.wireOp",EDGE,"E72.1");var subQ16=sQuery(id+"F12.wireOp",EDGE,"E74.1");var subQ18=sQuery(id+"F12.wireOp",EDGE,"E74.8");Q0=qUnion([makeQuery(id+"F12.imprint","IMPRINT",FACE,{"disambiguationData":[TD([[makeQuery(id+"F12.imprint","IMPRINT",EDGE,{"derivedFrom":subQ7}),1.0]])]}),makeQuery(id+"F12.imprint","IMPRINT",FACE,{"disambiguationData":[TD([[makeQuery(id+"F12.imprint","IMPRINT",EDGE,{"derivedFrom":subQ14}),1.0]])]}),makeQuery(id+"F12.imprint","IMPRINT",FACE,{"disambiguationData":[TD([[makeQuery(id+"F12.imprint","IMPRINT",EDGE,{"derivedFrom":subQ16}),1.0]])]}),makeQuery(id+"F12.imprint","IMPRINT",FACE,{"disambiguationData":[TD([[makeQuery(id+"F12.imprint","IMPRINT",EDGE,{"derivedFrom":subQ18}),-1.0]])]})]);}
            var Q1;
            Q1=makeQuery(id+"F5.boolean.opBoolean","SPLIT",FACE,{"disambiguationData":[TD([makeQuery(id+"F5.opExtrude","SWEPT_FACE",FACE,{"disambiguationData":[OSD([sQuery(id+"F4.wireOp",EDGE,"E41")])]})])],"derivedFrom":makeQuery(id+"F3.boolean.opBoolean","COPY",FACE,{"derivedFrom":makeQuery(id+"F3.opExtrude","CAP_FACE",FACE,{"disambiguationData":[OSD([sQuery(id+"F0.wireOp",EDGE,"E25.0"),sQuery(id+"F0.wireOp",EDGE,"E25.1"),sQuery(id+"F0.wireOp",EDGE,"E25.2"),sQuery(id+"F0.wireOp",EDGE,"E25.3"),sQuery(id+"F0.wireOp",EDGE,"E25.4"),sQuery(id+"F0.wireOp",EDGE,"E25.5"),sQuery(id+"F0.wireOp",EDGE,"E25.6"),sQuery(id+"F0.wireOp",EDGE,"E25.7")])],"isStart":false})})});
            extrude(context, id + "F13", {"entities" : qUnion([Q0]), "operationType" : NewBodyOperationType.REMOVE, "endBound" : BoundingType.UP_TO_SURFACE, "endBoundEntityFace" : qUnion([Q1]), "depth" : 25 * mm});
        }
        {
            var Q0;
            Q0=makeQuery(id+"F3.boolean.opBoolean","COPY",EDGE,{"derivedFrom":makeQuery(id+"F3.opExtrude","CAP_EDGE",EDGE,{"disambiguationData":[OSD([sQuery(id+"F0.wireOp",EDGE,"E25.6")])],"isStart":false})});
            var Q1;
            Q1=makeQuery(id+"F8.boolean.opBoolean","INTERSECT",EDGE,{"derivedFrom":[makeQuery(id+"F5.opExtrude","SWEPT_FACE",FACE,{"disambiguationData":[OSD([sQuery(id+"F4.wireOp",EDGE,"E30")])]}),makeQuery(id+"F8.opExtrude","CAP_FACE",FACE,{"disambiguationData":[OSD([sQuery(id+"F7.wireOp",EDGE,"E67")])],"isStart":false})]});
            var Q2;
            Q2=makeQuery(id+"F8.boolean.opBoolean","INTERSECT",EDGE,{"disambiguationData":[OD(1.0)],"derivedFrom":[makeQuery(id+"F5.opExtrude","SWEPT_FACE",FACE,{"disambiguationData":[OSD([sQuery(id+"F4.wireOp",EDGE,"E30")])]}),makeQuery(id+"F8.opExtrude","SWEPT_FACE",FACE,{"disambiguationData":[OSD([sQuery(id+"F7.wireOp",EDGE,"E67")])]})]});
            var Q3;
            {var subQ0=sQuery(id+"F4.wireOp",EDGE,"E30");Q3=makeQuery(id+"F8.boolean.opBoolean","SPLIT",EDGE,{"disambiguationData":[TD([makeQuery(id+"F5.opExtrude","SWEPT_FACE",FACE,{"disambiguationData":[OSD([sQuery(id+"F4.wireOp",EDGE,"E35.filletArc")])]})])],"derivedFrom":makeQuery(id+"F5.opExtrude","CAP_EDGE",EDGE,{"disambiguationData":[OSD([subQ0])],"isStart":false})});}
            var Q4;
            {var subQ0=sQuery(id+"F0.wireOp",EDGE,"E25.7");var subQ1=sQuery(id+"F0.wireOp",EDGE,"E25.1");var subQ2=sQuery(id+"F0.wireOp",EDGE,"E25.6");var subQ3=sQuery(id+"F0.wireOp",EDGE,"E25.5");var subQ4=sQuery(id+"F0.wireOp",EDGE,"E25.4");var subQ5=sQuery(id+"F0.wireOp",EDGE,"E25.0");var subQ6=sQuery(id+"F0.wireOp",EDGE,"E25.2");var subQ7=sQuery(id+"F0.wireOp",EDGE,"E25.3");Q4=makeQuery(id+"F8.boolean.opBoolean","INTERSECT",EDGE,{"derivedFrom":[makeQuery(id+"F5.boolean.opBoolean","SPLIT",FACE,{"disambiguationData":[TD([makeQuery(id+"F2.opExtrude","SWEPT_FACE",FACE,{"disambiguationData":[OSD([subQ5])]})])],"derivedFrom":makeQuery(id+"F3.boolean.opBoolean","COPY",FACE,{"derivedFrom":makeQuery(id+"F3.opExtrude","CAP_FACE",FACE,{"disambiguationData":[OSD([subQ5,subQ1,subQ6,subQ7,subQ4,subQ3,subQ2,subQ0])],"isStart":false})})}),makeQuery(id+"F8.opExtrude","SWEPT_FACE",FACE,{"disambiguationData":[OSD([sQuery(id+"F7.wireOp",EDGE,"E67")])]})]});}
            var Q5;
            Q5=makeQuery(id+"F8.boolean.opBoolean","INTERSECT",EDGE,{"disambiguationData":[OD(0.0)],"derivedFrom":[makeQuery(id+"F5.opExtrude","SWEPT_FACE",FACE,{"disambiguationData":[OSD([sQuery(id+"F4.wireOp",EDGE,"E30")])]}),makeQuery(id+"F8.opExtrude","SWEPT_FACE",FACE,{"disambiguationData":[OSD([sQuery(id+"F7.wireOp",EDGE,"E67")])]})]});
            fillet(context, id + "F14", {"entities" : qUnion([Q0, Q1, Q2, Q3, Q4, Q5]), "radius" : 3 * mm, "tangentPropagation" : true, "allowEdgeOverflow" : false});
        }
        {
            var Q0;
            Q0=makeQuery(id+"F1.opExtrude","CAP_EDGE",EDGE,{"disambiguationData":[OSD([sQuery(id+"F0.wireOp",EDGE,"E1.bottom")])],"isStart":false});
            fillet(context, id + "F15", {"entities" : qUnion([Q0]), "radius" : 2 * mm, "tangentPropagation" : true, "allowEdgeOverflow" : false});
        }
        {
            var Q0;
            {var subQ0=sQuery(id+"F0.wireOp",EDGE,"E22.filletArc");var subQ1=sQuery(id+"F0.wireOp",EDGE,"E7");var subQ2=sQuery(id+"F0.wireOp",EDGE,"E6");var subQ3=sQuery(id+"F0.wireOp",EDGE,"E5");var subQ4=sQuery(id+"F0.wireOp",EDGE,"E4");var subQ5=sQuery(id+"F0.wireOp",EDGE,"E1.bottom");var subQ6=sQuery(id+"F0.wireOp",EDGE,"E21.filletArc");var subQ7=sQuery(id+"F0.wireOp",EDGE,"E1.top");var subQ8=sQuery(id+"F0.wireOp",EDGE,"E1.left");var subQ9=sQuery(id+"F0.wireOp",EDGE,"E1.right");var subQ10=sQuery(id+"F0.wireOp",EDGE,"E23.filletArc");var subQ11=sQuery(id+"F0.wireOp",EDGE,"E24.filletArc");Q0=makeQuery(id+"F2.boolean.opBoolean","SPLIT",FACE,{"disambiguationData":[TD([makeQuery(id+"F1.opExtrude","SWEPT_FACE",FACE,{"disambiguationData":[OSD([subQ5])]})])],"derivedFrom":makeQuery(id+"F1.opExtrude","CAP_FACE",FACE,{"disambiguationData":[OSD([subQ5,subQ7,subQ8,subQ9,subQ4,subQ3,subQ2,subQ1,subQ6,subQ0,subQ10,subQ11])],"isStart":true})});}
            var sketch = newSketch(context, id + "F16", { "sketchPlane" : qUnion([Q0])});
            skLineSegment(sketch, "E79", {"start": v(0, 90) * mm, "end": v(0, 120) * mm, "construction": true});
            skCircle(sketch, "E80", {"center": v(0, 120) * mm, "radius": 6 * mm});
            skArc(sketch, "E81", {"start": v(15, 120) * mm, "mid": v(0, 135) * mm, "end": v(-15, 120) * mm});
            skLineSegment(sketch, "E82", {"start": v(-15, 120) * mm, "end": v(-15, 108) * mm});
            skLineSegment(sketch, "E83", {"start": v(15, 120) * mm, "end": v(15, 108) * mm});
            skLineSegment(sketch, "E84", {"start": v(-15, 108) * mm, "end": v(-33, 90) * mm});
            skLineSegment(sketch, "E85", {"start": v(15, 108) * mm, "end": v(33, 90) * mm});
            skLineSegment(sketch, "E86", {"start": v(-80, 0) * mm, "end": v(80, 0) * mm, "construction": true});
            skLineSegment(sketch, "E87.MirrorCS", {"start": v(-15, -108) * mm, "end": v(-33, -90) * mm});
            skLineSegment(sketch, "E88.MirrorCS", {"start": v(-15, -120) * mm, "end": v(-15, -108) * mm});
            skArc(sketch, "E89.MirrorCS", {"start": v(15, -120) * mm, "mid": v(0, -135) * mm, "end": v(-15, -120) * mm});
            skLineSegment(sketch, "E90.MirrorCS", {"start": v(15, -120) * mm, "end": v(15, -108) * mm});
            skLineSegment(sketch, "E91.MirrorCS", {"start": v(15, -108) * mm, "end": v(33, -90) * mm});
            skCircle(sketch, "E92.MirrorC", {"center": v(0, -120) * mm, "radius": 6 * mm});
            skLineSegment(sketch, "E93.MirrorCS", {"start": v(0, -90) * mm, "end": v(0, -120) * mm, "construction": true});
            skSolve(sketch);
        }
        {
            var Q0;
            Q0=makeQuery(id+"F16.imprint","IMPRINT",FACE,{"disambiguationData":[TD([[makeQuery(id+"F16.imprint","IMPRINT",EDGE,{"derivedFrom":sQuery(id+"F16.wireOp",EDGE,"388f877d-5262-4f45-91ee-3bcb61d2029e0.MirrorCS")}),-1.0]])]});
            var Q1;
            Q1=makeQuery(id+"F16.imprint","IMPRINT",FACE,{"disambiguationData":[TD([[makeQuery(id+"F16.imprint","IMPRINT",EDGE,{"derivedFrom":makeQuery(id+"F1.opExtrude","CAP_EDGE",EDGE,{"disambiguationData":[OSD([sQuery(id+"F0.wireOp",EDGE,"E1.left")])],"isStart":true})}),-1.0]])]});
            var Q2;
            Q2=makeQuery(id+"F16.imprint","IMPRINT",FACE,{"disambiguationData":[TD([[makeQuery(id+"F16.imprint","IMPRINT",EDGE,{"derivedFrom":sQuery(id+"F16.wireOp",EDGE,"E80")}),-1.0]])]});
            var Q3;
            Q3=makeQuery(id+"F16.imprint","IMPRINT",FACE,{"disambiguationData":[TD([[makeQuery(id+"F16.imprint","IMPRINT",EDGE,{"derivedFrom":sQuery(id+"F16.wireOp",EDGE,"E81")}),1.0]])]});
            var Q4;
            {var subQ0=sQuery(id+"F16.wireOp",EDGE,"E87.MirrorCS");Q4=makeQuery(id+"F16.imprint","IMPRINT",FACE,{"disambiguationData":[TD([[makeQuery(id+"F16.imprint","IMPRINT",EDGE,{"derivedFrom":subQ0}),-1.0]])]});}
            var Q5;
            {var subQ0=sQuery(id+"F4.wireOp",EDGE,"E63.0.MirrorCS");var subQ1=sQuery(id+"F4.wireOp",EDGE,"E62.0.MirrorCS");var subQ2=sQuery(id+"F4.wireOp",EDGE,"E61.0.MirrorCS");var subQ3=sQuery(id+"F4.wireOp",EDGE,"E60.0.MirrorCS");var subQ4=sQuery(id+"F4.wireOp",EDGE,"E59.0.MirrorCS");var subQ5=sQuery(id+"F4.wireOp",EDGE,"E58.0.MirrorCS");var subQ6=sQuery(id+"F4.wireOp",EDGE,"E57.0.MirrorCS");var subQ7=sQuery(id+"F4.wireOp",EDGE,"E56.0.MirrorCS");var subQ8=sQuery(id+"F4.wireOp",EDGE,"E55.0.MirrorCS");var subQ9=sQuery(id+"F4.wireOp",EDGE,"E54.0.MirrorCS");var subQ10=sQuery(id+"F4.wireOp",EDGE,"E53.0.MirrorCS");var subQ11=sQuery(id+"F4.wireOp",EDGE,"E52.filletArc");var subQ12=sQuery(id+"F4.wireOp",EDGE,"E45");var subQ13=sQuery(id+"F4.wireOp",EDGE,"E43");var subQ14=sQuery(id+"F4.wireOp",EDGE,"E42");var subQ15=sQuery(id+"F4.wireOp",EDGE,"E41");var subQ16=sQuery(id+"F4.wireOp",EDGE,"E46");var subQ17=sQuery(id+"F4.wireOp",EDGE,"E47.filletArc");var subQ18=sQuery(id+"F4.wireOp",EDGE,"E48.filletArc");var subQ19=sQuery(id+"F4.wireOp",EDGE,"E49.filletArc");var subQ20=sQuery(id+"F4.wireOp",EDGE,"E50.filletArc");var subQ21=sQuery(id+"F4.wireOp",EDGE,"E51.filletArc");Q5=makeQuery(id+"F6.boolean.opBoolean","SPLIT",FACE,{"disambiguationData":[TD([makeQuery(id+"F5.opExtrude","SWEPT_FACE",FACE,{"disambiguationData":[OSD([subQ15])]})])],"derivedFrom":makeQuery(id+"F5.opExtrude","CAP_FACE",FACE,{"disambiguationData":[OSD([sQuery(id+"F4.wireOp",EDGE,"E27.0"),sQuery(id+"F4.wireOp",EDGE,"E28.0"),sQuery(id+"F4.wireOp",EDGE,"E29"),sQuery(id+"F4.wireOp",EDGE,"E30"),sQuery(id+"F4.wireOp",EDGE,"E33.filletArc"),sQuery(id+"F4.wireOp",EDGE,"E34.filletArc"),sQuery(id+"F4.wireOp",EDGE,"E35.filletArc"),sQuery(id+"F4.wireOp",EDGE,"E36.filletArc"),subQ15,subQ14,subQ13,subQ12,subQ16,subQ17,subQ18,subQ19,subQ20,subQ21,subQ11,subQ10,subQ9,subQ8,subQ7,subQ6,subQ5,subQ4,subQ3,subQ2,subQ1,subQ0])],"isStart":true})});}
            extrude(context, id + "F17", {"entities" : qUnion([Q0, Q1, Q2, Q3, Q4]), "endBound" : BoundingType.UP_TO_SURFACE, "endBoundEntityFace" : qUnion([Q5]), "depth" : 25 * mm});
        }
    });
